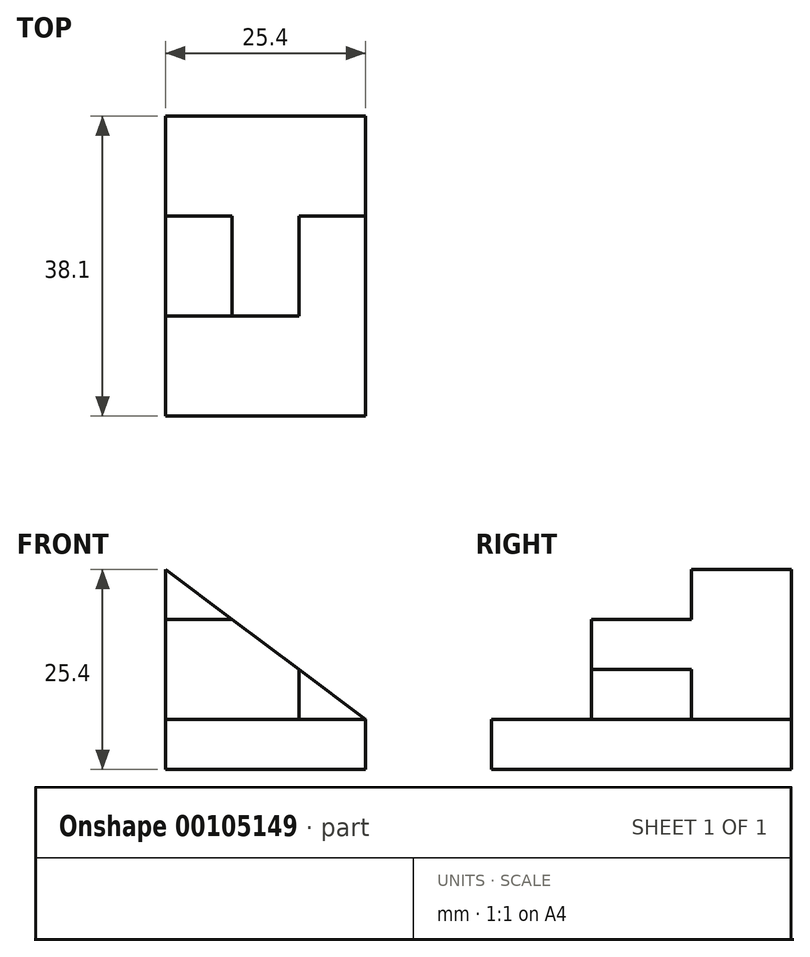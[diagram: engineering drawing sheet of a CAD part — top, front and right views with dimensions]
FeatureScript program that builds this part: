
annotation { "Feature Type Name" : "Feature", "Feature Type Description" : "" }
export const myFeature = defineFeature(function(context is Context, id is Id, definition is map)
    precondition{}
    {
        {
            var Q0;
            Q0=qCreatedBy(makeId("Top.planeOp"),FACE);
            var sketch = newSketch(context, id + "F0", { "sketchPlane" : qUnion([Q0])});
            skLineSegment(sketch, "E0.bottom", {"start": v(0, 0) * mm, "end": v(25.4, 0) * mm});
            skLineSegment(sketch, "E0.top", {"start": v(0, 38.1) * mm, "end": v(25.4, 38.1) * mm});
            skLineSegment(sketch, "E0.left", {"start": v(0, 0) * mm, "end": v(0, 38.1) * mm});
            skLineSegment(sketch, "E0.right", {"start": v(25.4, 0) * mm, "end": v(25.4, 38.1) * mm});
            skSolve(sketch);
        }
        {
            var Q0;
            Q0 = qSketchRegion(id + "F0", true);
            extrude(context, id + "F1", {"entities" : qUnion([Q0]), "depth" : 6.35 * mm});
        }
        {
            var Q0;
            Q0=qCreatedBy(makeId("Front.planeOp"),FACE);
            cPlane(context, id + "F2", {"entities" : qUnion([Q0]), "cplaneType" : CPlaneType.OFFSET, "offset" : 12.7 * mm, "oppositeDirection" : true, "width" : 152.4 * mm, "height" : 152.4 * mm});
        }
        {
            var Q0;
            Q0=qCreatedBy(id+"F2.planeOp",FACE);
            var sketch = newSketch(context, id + "F3", { "sketchPlane" : qUnion([Q0])});
            skLineSegment(sketch, "E1", {"start": v(0, 0) * mm, "end": v(0, 25.4) * mm});
            skLineSegment(sketch, "E2", {"start": v(0, 25.4) * mm, "end": v(25.4, 6.35) * mm});
            skLineSegment(sketch, "E3", {"start": v(25.4, 6.35) * mm, "end": v(25.4, 0) * mm});
            skLineSegment(sketch, "E4", {"start": v(25.4, 0) * mm, "end": v(0, 0) * mm});
            skSolve(sketch);
        }
        {
            var Q0;
            Q0 = qSketchRegion(id + "F3", true);
            extrude(context, id + "F4", {"entities" : qUnion([Q0]), "operationType" : NewBodyOperationType.ADD, "oppositeDirection" : true, "depth" : 25.4 * mm});
        }
        {
            var Q0;
            Q0=makeQuery(id+"F4.opExtrude","CAP_FACE",FACE,{"disambiguationData":[OSD([sQuery(id+"F3.wireOp",EDGE,"E1"),sQuery(id+"F3.wireOp",EDGE,"E2"),sQuery(id+"F3.wireOp",EDGE,"E3"),sQuery(id+"F3.wireOp",EDGE,"E4")])],"isStart":true});
            var sketch = newSketch(context, id + "F5", { "sketchPlane" : qUnion([Q0])});
            skLineSegment(sketch, "E5", {"start": v(0, 19.05) * mm, "end": v(8.47, 19.05) * mm});
            skLineSegment(sketch, "E6", {"start": v(8.47, 19.05) * mm, "end": v(0, 25.4) * mm});
            skLineSegment(sketch, "E7", {"start": v(0, 25.4) * mm, "end": v(0, 19.05) * mm});
            skLineSegment(sketch, "E8", {"start": v(16.93, 12.7) * mm, "end": v(16.93, 6.35) * mm});
            skLineSegment(sketch, "E9", {"start": v(16.93, 6.35) * mm, "end": v(25.4, 6.35) * mm});
            skLineSegment(sketch, "E10", {"start": v(25.4, 6.35) * mm, "end": v(16.93, 12.7) * mm});
            skSolve(sketch);
        }
        {
            var Q0;
            Q0 = qSketchRegion(id + "F5", true);
            extrude(context, id + "F6", {"entities" : qUnion([Q0]), "operationType" : NewBodyOperationType.REMOVE, "oppositeDirection" : true, "depth" : 12.7 * mm});
        }
    });
